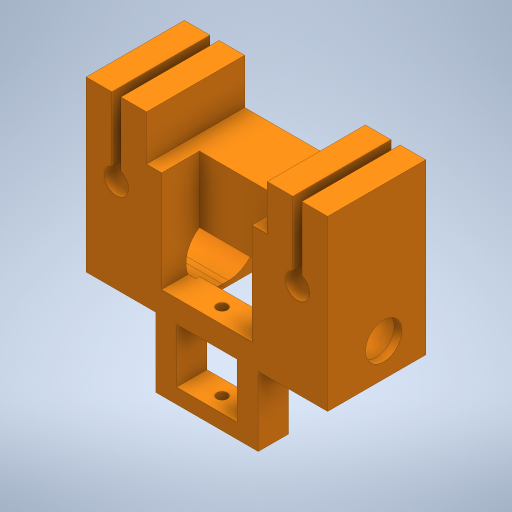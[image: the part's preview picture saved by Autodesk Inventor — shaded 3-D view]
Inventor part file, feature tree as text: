
AUTODESK INVENTOR PART (.ipt)
format: ipt  version: 2023 (Build 270158000, 158)  size: 573,440 bytes
history: native  units: mm
features: extrude x20, sketch x20, projected_geometry x9, plane x1
ambient origin geometry x8: Origin, YZ Plane, XZ Plane, XY Plane, X Axis, Y Axis, Z Axis, Center Point
bodies: Solid1 (feature_tree)
feature tree (50):
  extrude  "Extrusion1"  Depth=10.0mm
  extrude  "Extrusion5"  Depth=1.5mm
  extrude  "Extrusion11"  Depth=10.0mm
  extrude  "Extrusion13"  Depth=80.0mm
  extrude  "Extrusion14"  TaperAngle=0.0deg  [1 undecoded]
  extrude  "Extrusion15"  Depth=20.0mm
  extrude  "Extrusion16"  Depth=20.0mm
  extrude  "Extrusion17"  Depth=10.0mm
  extrude  "Extrusion18"  Depth=20.0mm
  plane  "Work Plane5"
  extrude  "Extrusion21"  Depth=35.0mm
  extrude  "Extrusion19"  Depth=80.0mm TaperAngle=0.0deg
  extrude  "Extrusion20"  Depth=25.0mm TaperAngle=0.0deg
  extrude  "Extrusion22"  Depth=5.0mm
  extrude  "Extrusion23"  Depth=6.0mm TaperAngle=0.0deg
  extrude  "Extrusion24"  Depth=30.0mm
  extrude  "Extrusion25"  Depth=15.0mm
  extrude  "Extrusion26"  Depth=37.0mm TaperAngle=0.0deg
  extrude  "Extrusion27"  Depth=7.0mm
  extrude  "Extrusion28"  Depth=18.0mm
  extrude  "Extrusion29"  Depth=23.0mm
  sketch  "Sketch1"  dims[d2=8.0mm d3=10.0mm]
  sketch  "Sketch5"  dims[d7=1.5mm d8=1.5mm]
  sketch  "Sketch13"  dims[d9=36.0mm d10=0.0mm d16=10.0mm]
  projected_geometry  "Projected Loop1"
  sketch  "Sketch16"  dims[d17=8.0mm d18=1.5mm d19=1.5mm d20=10.0mm d21=8.0mm d22=80.0mm]
  sketch  "Sketch17"  dims[d23=10.0mm d24=0.0mm]
  sketch  "Sketch18"  dims[d25=60.0mm d26=20.0mm]
  sketch  "Sketch19"  dims[d27=20.0mm d28=20.0mm]
  sketch  "Sketch20"  dims[d29=20.0mm d30=10.0mm]
  sketch  "Sketch21"  dims[d31=10.0mm d32=20.0mm]
  projected_geometry  "Projected Loop2"
  sketch  "Sketch22"  dims[d40=30.0mm d41=35.0mm]
  sketch  "Sketch24"  dims[d45=20.0mm d46=80.0mm d47=0.0mm]
  sketch  "Sketch25"  dims[d79=25.0mm d82=25.0mm d83=1.0mm d84=0.0mm]
  sketch  "Sketch26"  dims[d85=19.0mm d86=5.0mm]
  projected_geometry  "Projected Loop3"
  sketch  "Sketch27"  dims[d87=15.0mm d103=6.0mm d104=0.0mm]
  projected_geometry  "Projected Loop4"
  sketch  "Sketch28"  dims[d105=20.0mm d106=0.0mm d107=30.0mm]
  sketch  "Sketch29"  dims[d108=25.0mm d109=15.0mm]
  sketch  "Sketch30"  dims[d110=0.0mm d111=37.0mm d112=0.0mm]
  projected_geometry  "Projected Loop5"
  projected_geometry  "Projected Loop6"
  projected_geometry  "Projected Loop7"
  sketch  "Sketch31"  dims[d113=7.0mm d114=7.0mm]
  sketch  "Sketch32"  dims[d115=5.0mm d116=18.0mm]
  projected_geometry  "Projected Loop8"
  sketch  "Sketch33"  dims[d117=20.0mm d118=23.0mm d119=15.5mm d120=0.0mm d121=3.5mm d122=7.5mm d123=40.0mm d124=80.0mm d125=0.0mm d126=2.5mm d127=0.0mm d131=75.0mm d132=0.0mm d133=25.0mm d134=27.5mm d136=10.0mm d137=0.0mm d138=27.5mm d139=27.5mm d140=30.0mm d141=7.5mm d142=0.0mm d143=12.0mm d144=2.5mm d145=0.0mm d146=2.5mm d147=0.0mm d150=30.5mm d151=0.0mm d152=1.5mm d153=100.5mm d154=0.0mm d155=15.0mm d156=0.0mm d157=20.0mm d158=20.0mm d159=15.0mm d160=0.0mm d161=4.0mm d162=0.0mm d170=1.0mm d171=1.0mm d172=19.0mm d173=19.0mm d174=3.5mm d175=19.0mm d176=1.5mm d177=0.0mm]
  projected_geometry  "Projected Loop9"
note: 1 required parameter value undecoded (feature->parameter linkage not recoverable at this tier; creation-order binding heuristic only, values carry confidence <= 0.55)
